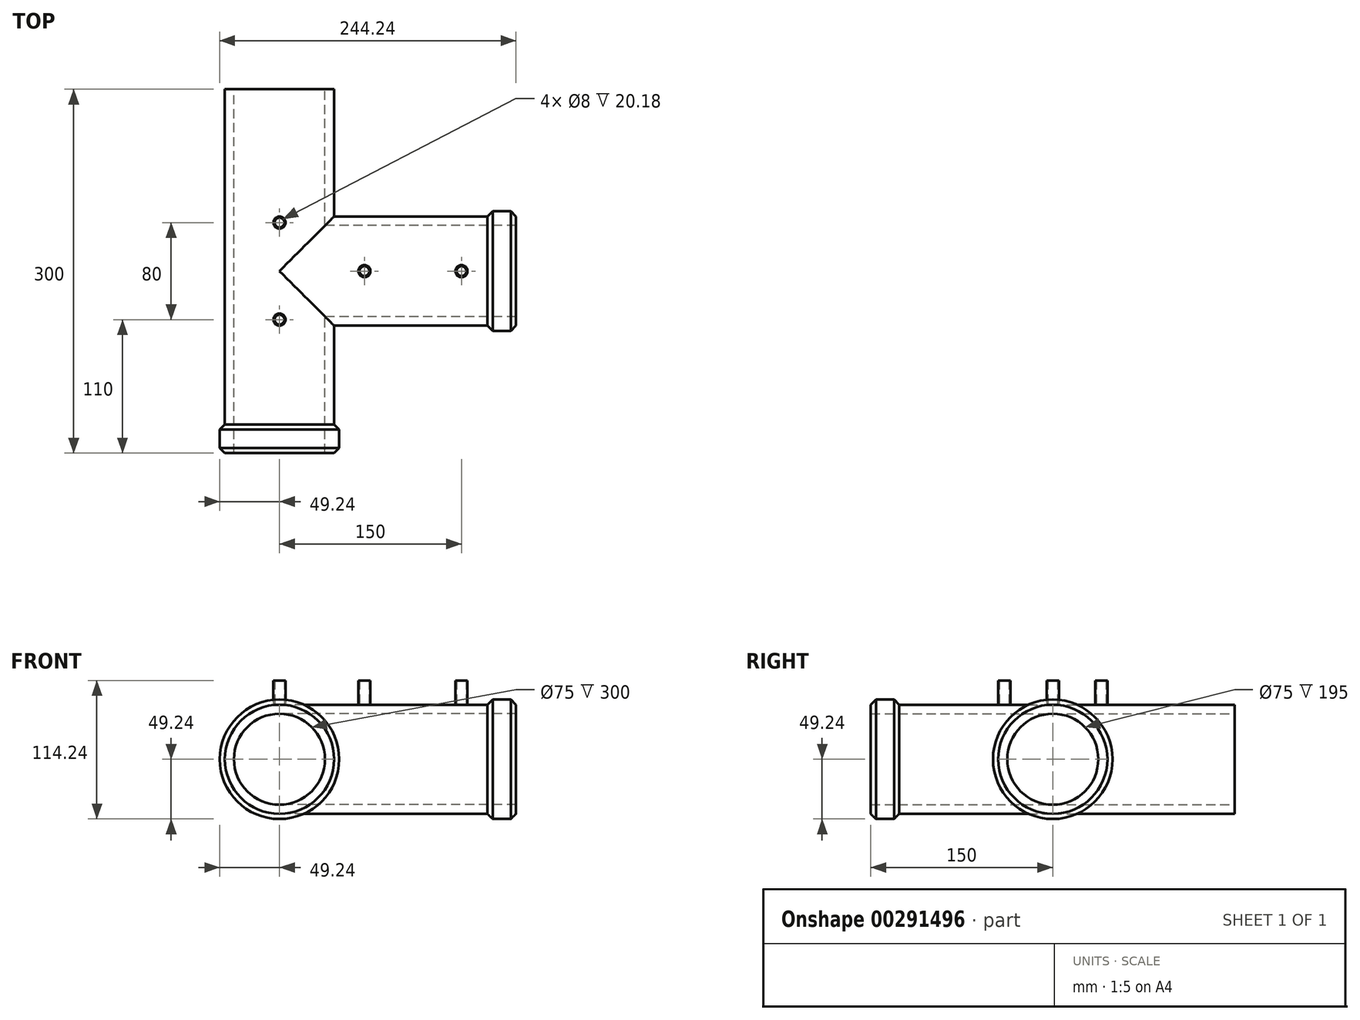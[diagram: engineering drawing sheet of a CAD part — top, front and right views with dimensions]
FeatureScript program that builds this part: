
annotation { "Feature Type Name" : "Feature", "Feature Type Description" : "" }
export const myFeature = defineFeature(function(context is Context, id is Id, definition is map)
    precondition{}
    {
        {
            var Q0;
            Q0=qCreatedBy(makeId("Front.planeOp"),FACE);
            var sketch = newSketch(context, id + "F0", { "sketchPlane" : qUnion([Q0])});
            skCircle(sketch, "E0", {"center": v(0, 0) * mm, "radius": 37.5 * mm});
            skCircle(sketch, "E1", {"center": v(0, 0) * mm, "radius": 45 * mm});
            skSolve(sketch);
        }
        {
            var Q0;
            Q0=makeQuery(id+"F0.imprint","IMPRINT",FACE,{"disambiguationData":[TD([[makeQuery(id+"F0.imprint","IMPRINT",EDGE,{"derivedFrom":sQuery(id+"F0.wireOp",EDGE,"E0")}),-1.0]])]});
            extrude(context, id + "F1", {"entities" : qUnion([Q0]), "endBound" : BoundingType.SYMMETRIC, "depth" : 300 * mm});
        }
        {
            var Q0;
            Q0=qCreatedBy(makeId("Top.planeOp"),FACE);
            cPlane(context, id + "F2", {"entities" : qUnion([Q0]), "cplaneType" : CPlaneType.OFFSET, "offset" : 45 * mm, "width" : 150 * mm, "height" : 150 * mm});
        }
        {
            var Q0;
            Q0=qCreatedBy(id+"F2.planeOp",FACE);
            var sketch = newSketch(context, id + "F3", { "sketchPlane" : qUnion([Q0])});
            skCircle(sketch, "E2", {"center": v(0, 40) * mm, "radius": 5 * mm});
            skCircle(sketch, "E3", {"center": v(0, -40) * mm, "radius": 5 * mm});
            skCircle(sketch, "E4", {"center": v(0, 40) * mm, "radius": 4 * mm});
            skCircle(sketch, "E5", {"center": v(0, -40) * mm, "radius": 4 * mm});
            skSolve(sketch);
        }
        {
            var Q0;
            Q0=makeQuery(id+"F3.imprint","IMPRINT",FACE,{"disambiguationData":[TD([[makeQuery(id+"F3.imprint","IMPRINT",EDGE,{"derivedFrom":sQuery(id+"F3.wireOp",EDGE,"E2")}),1.0]])]});
            var Q1;
            Q1=makeQuery(id+"F3.imprint","IMPRINT",FACE,{"disambiguationData":[TD([[makeQuery(id+"F3.imprint","IMPRINT",EDGE,{"derivedFrom":sQuery(id+"F3.wireOp",EDGE,"E3")}),1.0]])]});
            extrude(context, id + "F4", {"entities" : qUnion([Q0, Q1]), "operationType" : NewBodyOperationType.ADD, "depth" : 20 * mm, "hasSecondDirection" : true, "secondDirectionOppositeDirection" : true, "secondDirectionDepth" : 5 * mm});
        }
        {
            var Q0;
            Q0=qCreatedBy(makeId("Top.planeOp"),FACE);
            var sketch = newSketch(context, id + "F5", { "sketchPlane" : qUnion([Q0])});
            skLineSegment(sketch, "E6", {"start": v(45, 100) * mm, "end": v(45, -100) * mm});
            skLineSegment(sketch, "E7", {"start": v(-45, -150) * mm, "end": v(-45, 100) * mm});
            skLineSegment(sketch, "E8", {"start": v(-45, -150) * mm, "end": v(-49.24, -145.76) * mm});
            skLineSegment(sketch, "E9", {"start": v(-49.24, -145.76) * mm, "end": v(-49.24, -130.76) * mm});
            skLineSegment(sketch, "E10", {"start": v(-49.24, -130.76) * mm, "end": v(-45, -126.51) * mm});
            skLineSegment(sketch, "E11", {"start": v(-45, -150) * mm, "end": v(-45, -126.51) * mm});
            skLineSegment(sketch, "E12", {"start": v(0, -127.53) * mm, "end": v(0, 149.67) * mm, "construction": true});
            skSolve(sketch);
        }
        {
            var Q0;
            Q0=makeQuery(id+"F5.imprint","IMPRINT",FACE,{"disambiguationData":[TD([[makeQuery(id+"F5.imprint","IMPRINT",EDGE,{"derivedFrom":sQuery(id+"F5.wireOp",EDGE,"E8")}),-1.0]])]});
            var Q1;
            Q1=sQuery(id+"F5.wireOp",EDGE,"E12");
            revolve(context, id + "F6", {"operationType" : NewBodyOperationType.ADD, "entities" : qUnion([Q0]), "axis" : qUnion([Q1]), "revolveType" : RevolveType.FULL});
        }
        {
            var Q0;
            Q0=qCreatedBy(makeId("Right.planeOp"),FACE);
            cPlane(context, id + "F7", {"entities" : qUnion([Q0]), "cplaneType" : CPlaneType.OFFSET, "offset" : 45 * mm, "width" : 150 * mm, "height" : 150 * mm});
        }
        {
            var Q0;
            Q0=qCreatedBy(id+"F7.planeOp",FACE);
            var sketch = newSketch(context, id + "F8", { "sketchPlane" : qUnion([Q0])});
            skCircle(sketch, "E13", {"center": v(0, 0) * mm, "radius": 37.5 * mm});
            skLineSegment(sketch, "E14", {"start": v(-76.51, 45) * mm, "end": v(76.51, 45) * mm});
            skCircle(sketch, "E15", {"center": v(0, 0) * mm, "radius": 45 * mm});
            skSolve(sketch);
        }
        {
            var Q0;
            Q0=makeQuery(id+"F8.imprint","IMPRINT",FACE,{"disambiguationData":[TD([[makeQuery(id+"F8.imprint","IMPRINT",EDGE,{"derivedFrom":sQuery(id+"F8.wireOp",EDGE,"E13")}),-1.0]])]});
            extrude(context, id + "F9", {"entities" : qUnion([Q0]), "operationType" : NewBodyOperationType.ADD, "depth" : 150 * mm, "hasSecondDirection" : true, "secondDirectionOppositeDirection" : true, "secondDirectionDepth" : 45 * mm});
        }
        {
            var Q0;
            Q0=qCreatedBy(makeId("Front.planeOp"),FACE);
            var sketch = newSketch(context, id + "F10", { "sketchPlane" : qUnion([Q0])});
            skCircle(sketch, "E16.0", {"center": v(0, 0) * mm, "radius": 37.5 * mm});
            skSolve(sketch);
        }
        {
            var Q0;
            Q0=makeQuery(id+"F10.imprint","IMPRINT",FACE,{"disambiguationData":[TD([[makeQuery(id+"F10.imprint","IMPRINT",EDGE,{"derivedFrom":sQuery(id+"F10.wireOp",EDGE,"E16.0")}),1.0]])]});
            extrude(context, id + "F11", {"entities" : qUnion([Q0]), "operationType" : NewBodyOperationType.REMOVE, "endBound" : BoundingType.SYMMETRIC, "oppositeDirection" : true, "depth" : 300 * mm});
        }
        {
            var Q0;
            Q0=qCreatedBy(id+"F7.planeOp",FACE);
            var sketch = newSketch(context, id + "F12", { "sketchPlane" : qUnion([Q0])});
            skCircle(sketch, "E17.0", {"center": v(0, 0) * mm, "radius": 37.5 * mm});
            skSolve(sketch);
        }
        {
            var Q0;
            Q0 = qSketchRegion(id + "F12", true);
            extrude(context, id + "F13", {"entities" : qUnion([Q0]), "operationType" : NewBodyOperationType.REMOVE, "oppositeDirection" : true, "depth" : 45 * mm});
        }
        {
            var Q0;
            Q0=qCreatedBy(makeId("Top.planeOp"),FACE);
            var sketch = newSketch(context, id + "F14", { "sketchPlane" : qUnion([Q0])});
            skLineSegment(sketch, "E18", {"start": v(45, 45) * mm, "end": v(195, 45) * mm});
            skLineSegment(sketch, "E19", {"start": v(145, -45) * mm, "end": v(45, -45) * mm});
            skLineSegment(sketch, "E20", {"start": v(195, 45) * mm, "end": v(190.76, 49.24) * mm});
            skLineSegment(sketch, "E21", {"start": v(190.76, 49.24) * mm, "end": v(175.76, 49.24) * mm});
            skLineSegment(sketch, "E22", {"start": v(175.76, 49.24) * mm, "end": v(171.51, 45) * mm});
            skLineSegment(sketch, "E23", {"start": v(195, 45) * mm, "end": v(171.51, 45) * mm});
            skLineSegment(sketch, "E24", {"start": v(157.06, 0) * mm, "end": v(-74.22, 0) * mm, "construction": true});
            skSolve(sketch);
        }
        {
            var Q0;
            Q0=makeQuery(id+"F14.imprint","IMPRINT",FACE,{"disambiguationData":[TD([[makeQuery(id+"F14.imprint","IMPRINT",EDGE,{"derivedFrom":sQuery(id+"F14.wireOp",EDGE,"E20")}),1.0]])]});
            var Q1;
            Q1=sQuery(id+"F14.wireOp",EDGE,"E24");
            revolve(context, id + "F15", {"operationType" : NewBodyOperationType.ADD, "entities" : qUnion([Q0]), "axis" : qUnion([Q1]), "revolveType" : RevolveType.FULL});
        }
        {
            var Q0;
            Q0=qCreatedBy(id+"F2.planeOp",FACE);
            var sketch = newSketch(context, id + "F16", { "sketchPlane" : qUnion([Q0])});
            skCircle(sketch, "E25", {"center": v(150, 0) * mm, "radius": 5 * mm});
            skCircle(sketch, "E26", {"center": v(150, 0) * mm, "radius": 4 * mm});
            skCircle(sketch, "E27", {"center": v(70, 0) * mm, "radius": 5 * mm});
            skCircle(sketch, "E28", {"center": v(70, 0) * mm, "radius": 4 * mm});
            skSolve(sketch);
        }
        {
            var Q0;
            Q0=makeQuery(id+"F16.imprint","IMPRINT",FACE,{"disambiguationData":[TD([[makeQuery(id+"F16.imprint","IMPRINT",EDGE,{"derivedFrom":sQuery(id+"F16.wireOp",EDGE,"E25")}),1.0]])]});
            var Q1;
            Q1=makeQuery(id+"F16.imprint","IMPRINT",FACE,{"disambiguationData":[TD([[makeQuery(id+"F16.imprint","IMPRINT",EDGE,{"derivedFrom":sQuery(id+"F16.wireOp",EDGE,"E27")}),1.0]])]});
            extrude(context, id + "F17", {"entities" : qUnion([Q0, Q1]), "operationType" : NewBodyOperationType.ADD, "depth" : 20 * mm, "hasSecondDirection" : true, "secondDirectionOppositeDirection" : true, "secondDirectionDepth" : 5 * mm});
        }
    });
